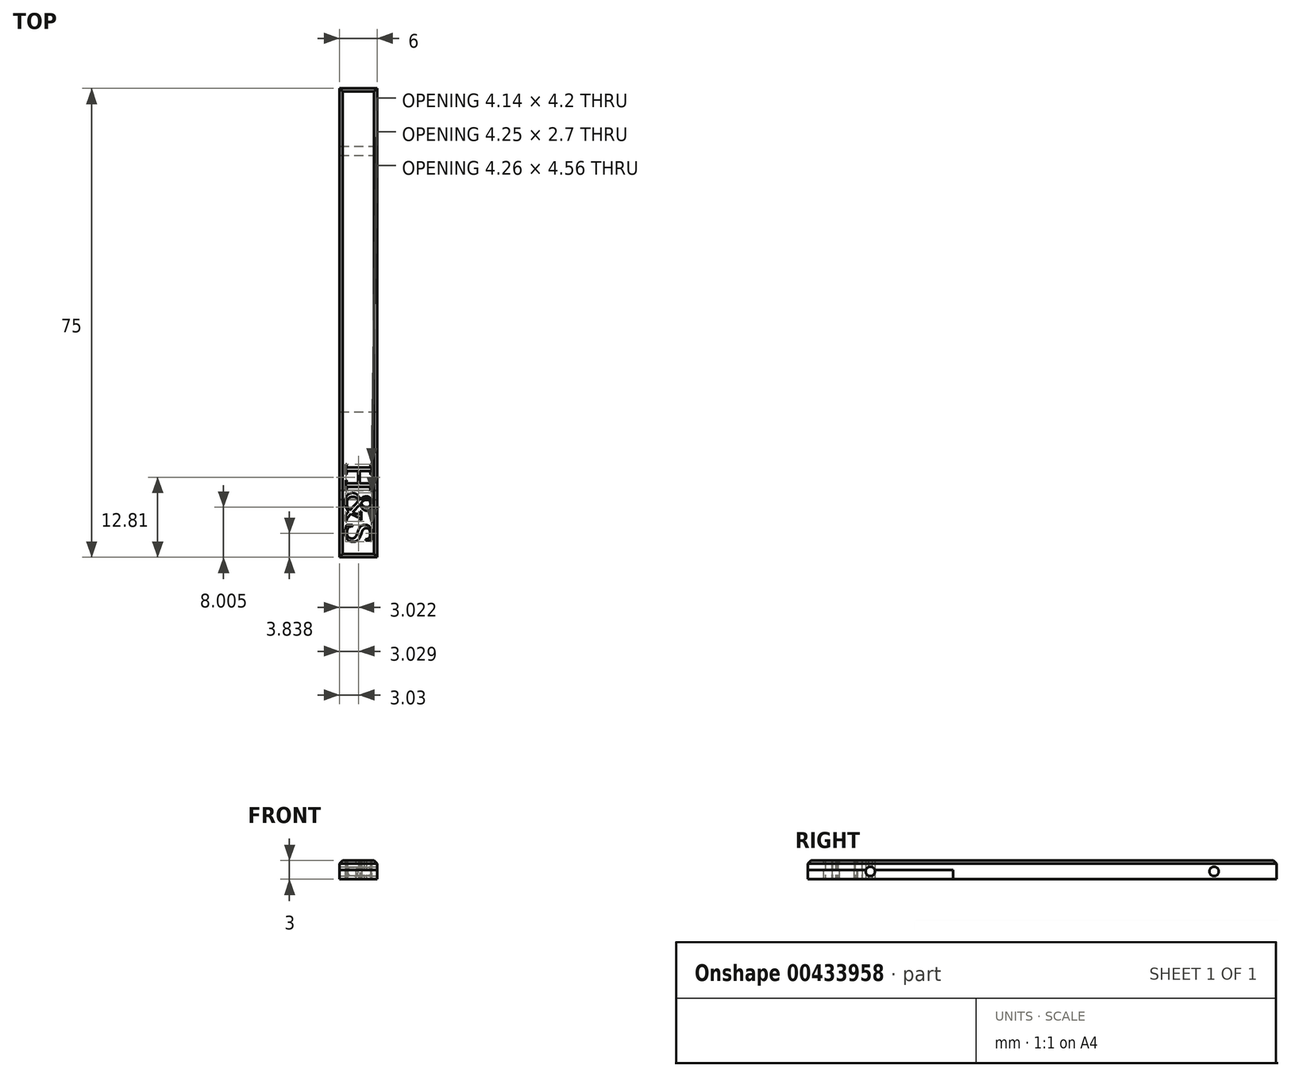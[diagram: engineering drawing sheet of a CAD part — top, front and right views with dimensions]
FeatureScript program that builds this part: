
annotation { "Feature Type Name" : "Feature", "Feature Type Description" : "" }
export const myFeature = defineFeature(function(context is Context, id is Id, definition is map)
    precondition{}
    {
        {
            var Q0;
            Q0=qCreatedBy(makeId("Top.planeOp"),FACE);
            var sketch = newSketch(context, id + "F0", { "sketchPlane" : qUnion([Q0])});
            skLineSegment(sketch, "E0.bottom", {"start": v(-1.74, 29.64) * mm, "end": v(4.26, 29.64) * mm});
            skLineSegment(sketch, "E0.top", {"start": v(-1.74, -45.36) * mm, "end": v(4.26, -45.36) * mm});
            skLineSegment(sketch, "E0.left", {"start": v(-1.74, 29.64) * mm, "end": v(-1.74, -45.36) * mm});
            skLineSegment(sketch, "E0.right", {"start": v(4.26, 29.64) * mm, "end": v(4.26, -45.36) * mm});
            skSolve(sketch);
        }
        {
            var Q0;
            Q0=makeQuery(id+"F0.imprint","IMPRINT",FACE,{"disambiguationData":[TD([[makeQuery(id+"F0.imprint","IMPRINT",EDGE,{"derivedFrom":sQuery(id+"F0.wireOp",EDGE,"E0.bottom")}),-1.0]])]});
            extrude(context, id + "F1", {"entities" : qUnion([Q0]), "depth" : 3 * mm});
        }
        {
            var Q0;
            Q0=qCreatedBy(makeId("Top.planeOp"),FACE);
            var sketch = newSketch(context, id + "F2", { "sketchPlane" : qUnion([Q0])});
            skText(sketch, "E1", { "text": "H&S", "fontName": "Tinos-Regular.ttf"});
            const initialGuessF2  = {"E1": [-0.00078, -0.03027, 0, -1, 0.00455]};
            skSetInitialGuess(sketch, initialGuessF2);
            skSolve(sketch);
        }
        {
            var Q0;
            Q0 = qSketchRegion(id + "F2", true);
            extrude(context, id + "F3", {"entities" : qUnion([Q0]), "operationType" : NewBodyOperationType.REMOVE, "depth" : 28.9 * mm});
        }
        {
            var Q0;
            {var subQ0=sQuery(id+"F0.wireOp",EDGE,"E0.left");var subQ1=sQuery(id+"F0.wireOp",EDGE,"E0.bottom");var subQ2=sQuery(id+"F0.wireOp",EDGE,"E0.right");var subQ3=sQuery(id+"F0.wireOp",EDGE,"E0.top");Q0=makeQuery(id+"F3.boolean.opBoolean","SPLIT",FACE,{"disambiguationData":[TD([makeQuery(id+"F1.opExtrude","SWEPT_FACE",FACE,{"disambiguationData":[OSD([subQ1])]})])],"derivedFrom":makeQuery(id+"F1.opExtrude","CAP_FACE",FACE,{"disambiguationData":[OSD([subQ1,subQ3,subQ0,subQ2])],"isStart":true})});}
            var sketch = newSketch(context, id + "F4", { "sketchPlane" : qUnion([Q0])});
            skLineSegment(sketch, "E2.bottom", {"start": v(-1.74, 45.36) * mm, "end": v(4.26, 45.36) * mm});
            skLineSegment(sketch, "E2.top", {"start": v(-1.74, 22.09) * mm, "end": v(4.26, 22.09) * mm});
            skLineSegment(sketch, "E2.left", {"start": v(-1.74, 45.36) * mm, "end": v(-1.74, 22.09) * mm});
            skLineSegment(sketch, "E2.right", {"start": v(4.26, 45.36) * mm, "end": v(4.26, 22.09) * mm});
            skSolve(sketch);
        }
        {
            var Q0;
            Q0 = qSketchRegion(id + "F4", true);
            extrude(context, id + "F5", {"entities" : qUnion([Q0]), "oppositeDirection" : true, "depth" : 1.5 * mm});
        }
        {
            var Q0;
            Q0=makeQuery(id+"F1.opExtrude","CAP_EDGE",EDGE,{"disambiguationData":[OSD([sQuery(id+"F0.wireOp",EDGE,"E0.left")])],"isStart":false});
            var Q1;
            Q1=makeQuery(id+"F1.opExtrude","CAP_EDGE",EDGE,{"disambiguationData":[OSD([sQuery(id+"F0.wireOp",EDGE,"E0.right")])],"isStart":false});
            chamfer(context, id + "F6", {"entities" : qUnion([Q0, Q1]), "width" : .5 * mm, "tangentPropagation" : true});
        }
        {
            var Q0;
            Q0=makeQuery(id+"F1.opExtrude","CAP_EDGE",EDGE,{"disambiguationData":[OSD([sQuery(id+"F0.wireOp",EDGE,"E0.top")])],"isStart":false});
            chamfer(context, id + "F7", {"entities" : qUnion([Q0]), "width" : .5 * mm, "tangentPropagation" : true});
        }
        {
            var Q0;
            Q0=makeQuery(id+"F1.opExtrude","CAP_EDGE",EDGE,{"disambiguationData":[OSD([sQuery(id+"F0.wireOp",EDGE,"E0.bottom")])],"isStart":false});
            chamfer(context, id + "F8", {"entities" : qUnion([Q0]), "width" : .5 * mm, "tangentPropagation" : true});
        }
        {
            var Q0;
            Q0=makeQuery(id+"F1.opExtrude","SWEPT_FACE",FACE,{"disambiguationData":[OSD([sQuery(id+"F0.wireOp",EDGE,"E0.right")])]});
            var sketch = newSketch(context, id + "F9", { "sketchPlane" : qUnion([Q0])});
            skCircle(sketch, "E3", {"center": v(19.64, 1.25) * mm, "radius": 0.75 * mm});
            skPoint(sketch, "E3.centerSnap0", {"position": v(29.64, 1.25) * mm});
            skCircle(sketch, "E4", {"center": v(-35.36, 1.25) * mm, "radius": 0.75 * mm});
            skSolve(sketch);
        }
        {
            var Q0;
            Q0=makeQuery(id+"F9.imprint","IMPRINT",FACE,{"disambiguationData":[TD([[makeQuery(id+"F9.imprint","IMPRINT",EDGE,{"derivedFrom":sQuery(id+"F9.wireOp",EDGE,"E3")}),1.0]])]});
            var Q1;
            Q1=makeQuery(id+"F9.imprint","IMPRINT",FACE,{"disambiguationData":[TD([[makeQuery(id+"F9.imprint","IMPRINT",EDGE,{"derivedFrom":sQuery(id+"F9.wireOp",EDGE,"E4")}),1.0]])]});
            extrude(context, id + "F10", {"entities" : qUnion([Q0, Q1]), "operationType" : NewBodyOperationType.REMOVE, "endBound" : BoundingType.THROUGH_ALL, "oppositeDirection" : true, "depth" : 25 * mm, "offsetDistance" : 25 * mm});
        }
    });
